# Revit family: Podajnik_recznikow_ZZ HIT
name_source: partatom
category: Furniture
units: mm (PartAtom-declared; Revit-internal decimal feet)

## family parameters
Always vertical = Yes
Cut with Voids When Loaded = No
Host = Wall
Room Calculation Point = No
Shared = No

## types (1)
- Type 1
    Depth / Glebokosc = 120 mm  [stored 0.393701 ft]
    Description = Podajnik ZZ HIT to pojemny, uniwersalny dozownik jednorazowych ręczników papierowych, który jest montowany na ścianie i zamykany na kluczyk. Stal nierdzewna, z której został wykonany, gwarantuje jego wytrzymałość i odporność na uszkodzenia. Matowe wykończenie oraz duża pojemność sprawiają, że pojemnik ma zastosowanie w różnorodnych obiektach użyteczności publicznej o dużym natężeniu ruchu. Wizjer w kształcie litery „S” umożliwia wygodne sprawdzanie poziomu ręczników w podajniku, co zwiększa jego funkcjonalność. Dozownik ręczników HIT to wysokiej jakości model, który gwarantuje zadowolenie użytkowników.
    Height / Wysokosc = 270 mm  [stored 0.885827 ft]
    Manufacturer = FANECO.com
    Manufacturer code / Kod producenta = 5901764292302
    Material = Stal nierdzewna szczotkowana
    Material finish / Wykonczenie = Stal nierdzewna 430 szczotkowana
    Model = HIT
    Product code / Kod produktu = P600SJB
    URL = https://faneco.com
    Weight / Waga = 1.8 kg
    Width / Szerokosc = 270 mm  [stored 0.885827 ft]

note: [stored X ft] marks values corroborated as IEEE doubles in the binary element streams (Revit-internal decimal feet)

## geometry (parser evidence)
native form markers: Sweep x8
no freeform markers — native parametric forms only
